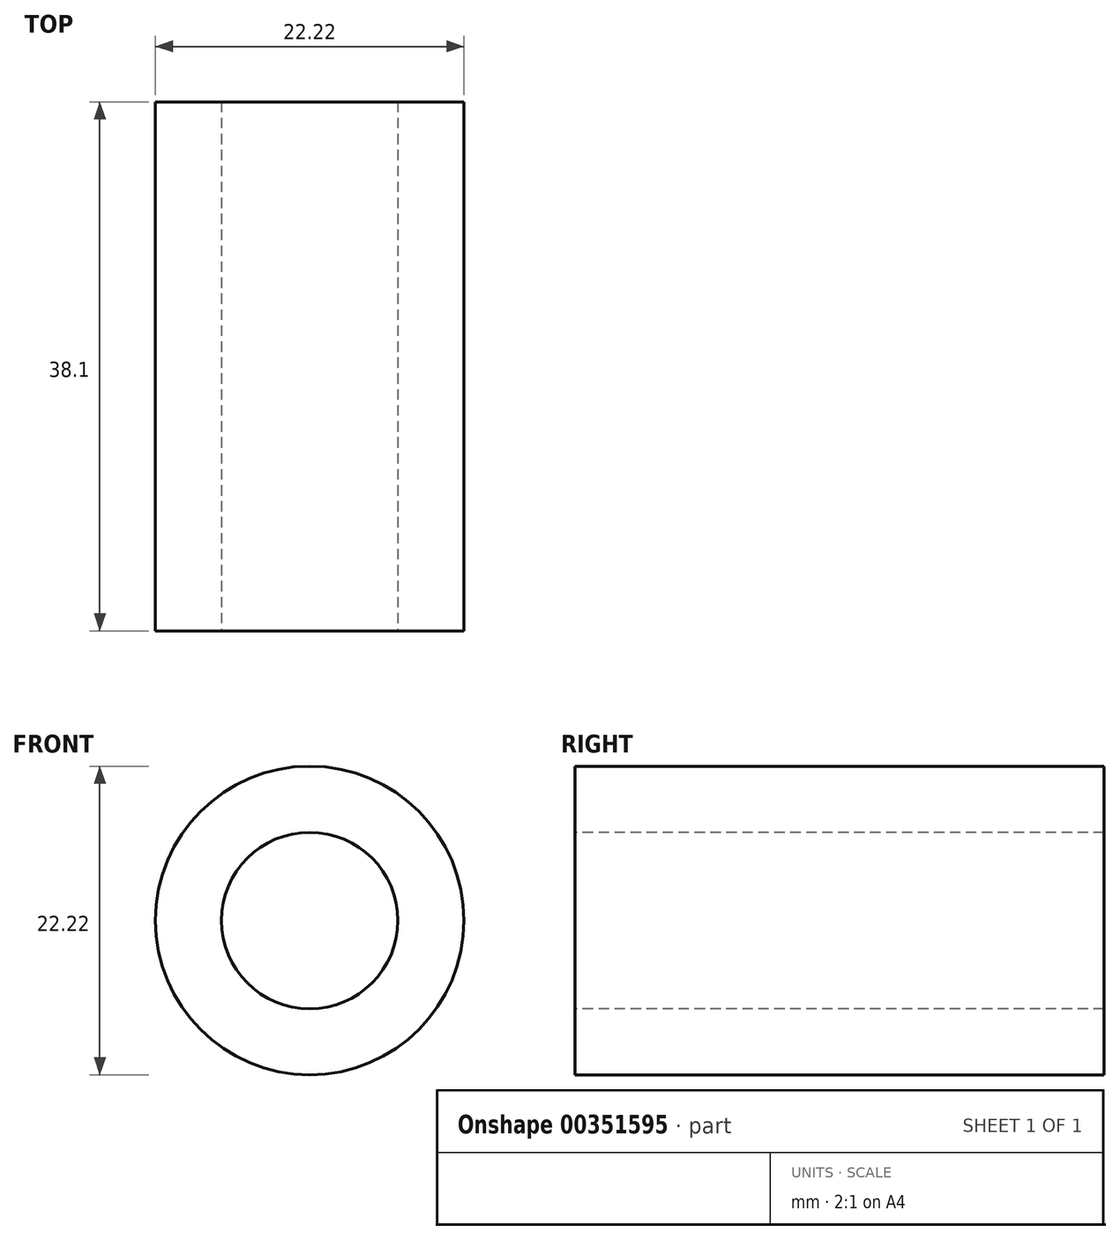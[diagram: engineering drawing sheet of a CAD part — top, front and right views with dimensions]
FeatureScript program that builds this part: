
annotation { "Feature Type Name" : "Feature", "Feature Type Description" : "" }
export const myFeature = defineFeature(function(context is Context, id is Id, definition is map)
    precondition{}
    {
        {
            var Q0;
            Q0=qCreatedBy(makeId("Front.planeOp"),FACE);
            var sketch = newSketch(context, id + "F0", { "sketchPlane" : qUnion([Q0])});
            skCircle(sketch, "E0", {"center": v(0, 0) * mm, "radius": 11.11 * mm});
            skSolve(sketch);
        }
        {
            var Q0;
            Q0 = qSketchRegion(id + "F0", true);
            extrude(context, id + "F1", {"entities" : qUnion([Q0]), "depth" : 38.1 * mm, "symmetric" : true});
        }
        {
            var Q0;
            Q0=makeQuery(id+"F1.opExtrude","CAP_FACE",FACE,{"disambiguationData":[OSD([sQuery(id+"F0.wireOp",EDGE,"E0")])],"isStart":false});
            var sketch = newSketch(context, id + "F2", { "sketchPlane" : qUnion([Q0])});
            skCircle(sketch, "E1", {"center": v(0, 0) * mm, "radius": 6.35 * mm});
            skSolve(sketch);
        }
        {
            var Q0;
            Q0 = qSketchRegion(id + "F2", true);
            var Q1;
            Q1=makeQuery(id+"F1.opExtrude","CAP_FACE",FACE,{"disambiguationData":[OSD([sQuery(id+"F0.wireOp",EDGE,"E0")])],"isStart":true});
            extrude(context, id + "F3", {"entities" : qUnion([Q0]), "operationType" : NewBodyOperationType.REMOVE, "endBound" : BoundingType.UP_TO_SURFACE, "oppositeDirection" : true, "endBoundEntityFace" : qUnion([Q1]), "depth" : 25.4 * mm});
        }
    });
